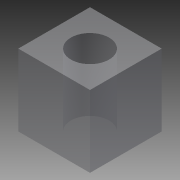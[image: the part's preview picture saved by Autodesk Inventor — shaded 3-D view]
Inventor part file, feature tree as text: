
AUTODESK INVENTOR PART (.ipt)
format: ipt  version: 2013 (Build 170138000, 138)  size: 77,312 bytes
history: native  units: in
note: dims shown in document units (in); Inventor stores cm internally (conversion verified against a paired STEP export)
features: extrude x1, sketch x1
ambient origin geometry x8: Origin, YZ Plane, XZ Plane, XY Plane, X Axis, Y Axis, Z Axis, Center Point
bodies: Solid1 (feature_tree)
feature tree (2):
  extrude  "Extrusion1"  Depth=0.5in
  sketch  "Sketch1"  dims[d0=0.5in d2=0.5in d3=0.266in d4=0.5in d5=0.0in]
